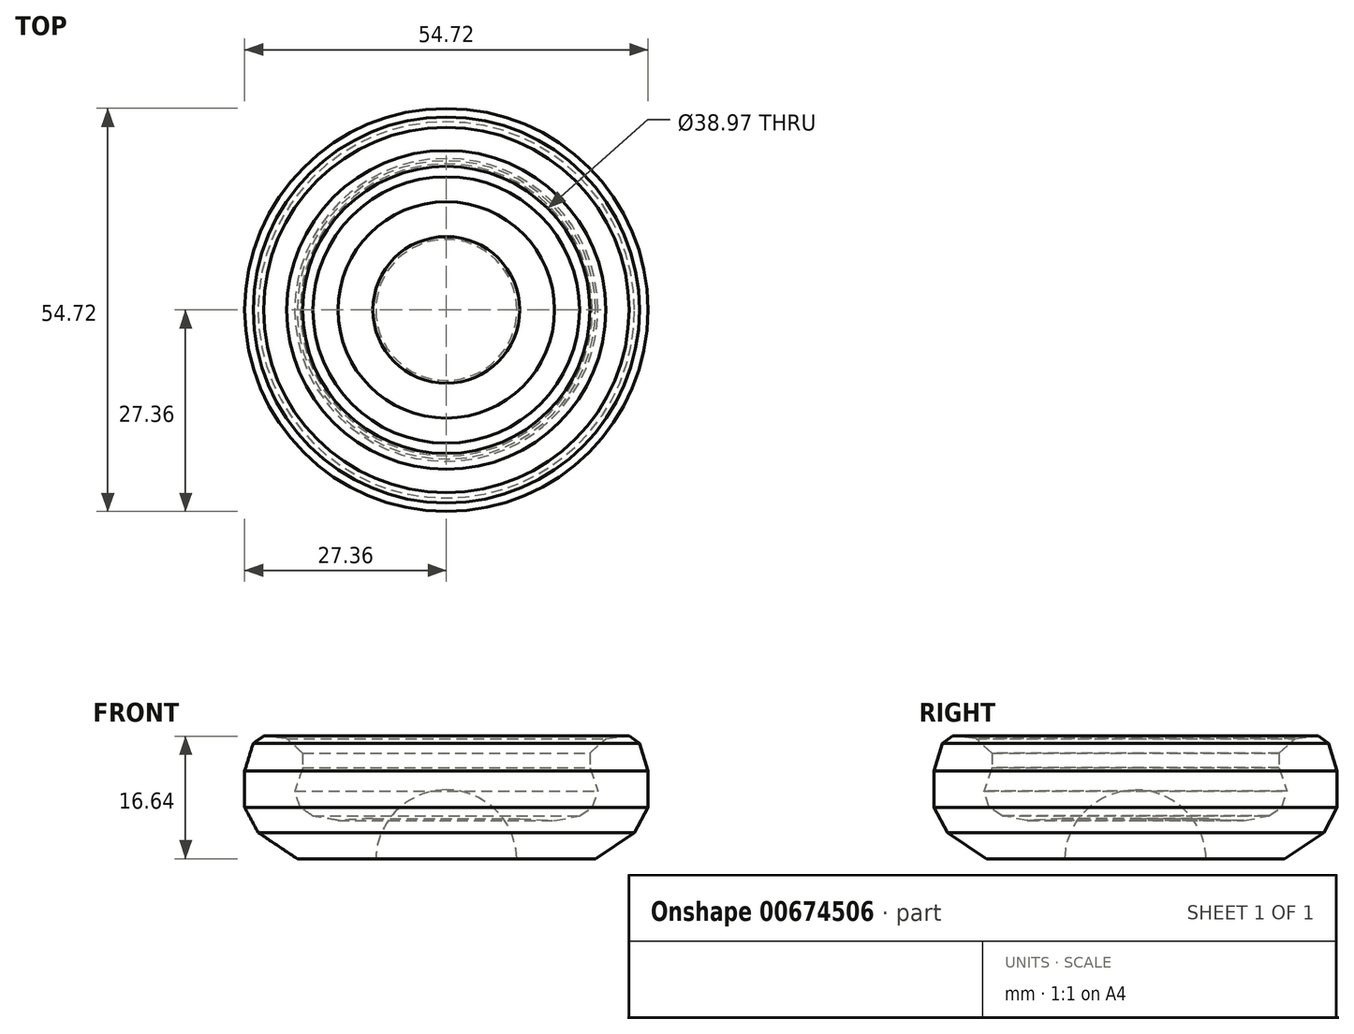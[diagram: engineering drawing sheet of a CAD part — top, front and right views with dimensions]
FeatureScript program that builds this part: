
annotation { "Feature Type Name" : "Feature", "Feature Type Description" : "" }
export const myFeature = defineFeature(function(context is Context, id is Id, definition is map)
    precondition{}
    {
        {
            var Q0;
            Q0=qCreatedBy(makeId("Front.planeOp"),FACE);
            var sketch = newSketch(context, id + "F0", { "sketchPlane" : qUnion([Q0])});
            skLineSegment(sketch, "E0", {"start": v(0, 0) * mm, "end": v(-20.23, 0) * mm});
            skLineSegment(sketch, "E1", {"start": v(-20.23, 0) * mm, "end": v(-25.53, 3.55) * mm});
            skLineSegment(sketch, "E2", {"start": v(-25.53, 3.55) * mm, "end": v(-27.36, 6.95) * mm});
            skLineSegment(sketch, "E3", {"start": v(-27.36, 6.95) * mm, "end": v(-27.36, 11.92) * mm});
            skLineSegment(sketch, "E4", {"start": v(-27.36, 11.92) * mm, "end": v(-26.2, 15.65) * mm});
            skLineSegment(sketch, "E5", {"start": v(-26.2, 15.65) * mm, "end": v(-24.79, 16.64) * mm});
            skLineSegment(sketch, "E6", {"start": v(-24.79, 16.64) * mm, "end": v(-21.64, 16.31) * mm});
            skLineSegment(sketch, "E7", {"start": v(-21.64, 16.31) * mm, "end": v(-19.49, 14.32) * mm});
            skLineSegment(sketch, "E8", {"start": v(-19.49, 14.32) * mm, "end": v(-19.49, 12.34) * mm});
            skLineSegment(sketch, "E9", {"start": v(-19.49, 12.34) * mm, "end": v(-20.56, 9.19) * mm});
            skLineSegment(sketch, "E10", {"start": v(-20.56, 9.19) * mm, "end": v(-19.82, 6.95) * mm});
            skLineSegment(sketch, "E11", {"start": v(-19.82, 6.95) * mm, "end": v(-18.08, 5.8) * mm});
            skLineSegment(sketch, "E12", {"start": v(-18.08, 5.8) * mm, "end": v(-14.68, 5.21) * mm});
            skLineSegment(sketch, "E13", {"start": v(-14.68, 5.21) * mm, "end": v(-9.96, 5.46) * mm});
            skLineSegment(sketch, "E14", {"start": v(-9.96, 5.46) * mm, "end": v(0, 5.46) * mm});
            skLineSegment(sketch, "E15", {"start": v(0, 5.46) * mm, "end": v(0, 0) * mm});
            skSolve(sketch);
        }
        {
            var Q0;
            Q0=sQuery(id+"F0.wireOp",EDGE,"E0");
            var Q1;
            Q1=sQuery(id+"F0.wireOp",EDGE,"E1");
            var Q2;
            Q2=sQuery(id+"F0.wireOp",EDGE,"E2");
            var Q3;
            Q3=sQuery(id+"F0.wireOp",EDGE,"E3");
            var Q4;
            Q4=sQuery(id+"F0.wireOp",EDGE,"E4");
            var Q5;
            Q5=sQuery(id+"F0.wireOp",EDGE,"E5");
            var Q6;
            Q6=sQuery(id+"F0.wireOp",EDGE,"E6");
            var Q7;
            Q7=sQuery(id+"F0.wireOp",EDGE,"E7");
            var Q8;
            Q8=sQuery(id+"F0.wireOp",EDGE,"E8");
            var Q9;
            Q9=sQuery(id+"F0.wireOp",EDGE,"E9");
            var Q10;
            Q10=sQuery(id+"F0.wireOp",EDGE,"E10");
            var Q11;
            Q11=sQuery(id+"F0.wireOp",EDGE,"E11");
            var Q12;
            Q12=sQuery(id+"F0.wireOp",EDGE,"E12");
            var Q13;
            Q13=sQuery(id+"F0.wireOp",EDGE,"E13");
            var Q14;
            Q14=sQuery(id+"F0.wireOp",EDGE,"E14");
            var Q15;
            Q15=sQuery(id+"F0.wireOp",EDGE,"E15");
            revolve(context, id + "F1", {"bodyType" : ToolBodyType.SURFACE, "surfaceEntities" : qUnion([Q0, Q1, Q2, Q3, Q4, Q5, Q6, Q7, Q8, Q9, Q10, Q11, Q12, Q13, Q14]), "axis" : qUnion([Q15]), "revolveType" : RevolveType.FULL});
        }
        {
            var Q0;
            Q0=qCreatedBy(makeId("Front.planeOp"),FACE);
            var sketch = newSketch(context, id + "F2", { "sketchPlane" : qUnion([Q0])});
            skLineSegment(sketch, "E16", {"start": v(0, 0) * mm, "end": v(-9.56, 0) * mm});
            skLineSegment(sketch, "E17", {"start": v(0, 0) * mm, "end": v(0, 9.35) * mm});
            skArc(sketch, "E18", {"start": v(0, 9.35) * mm, "mid": v(-6.68, 6.62) * mm, "end": v(-9.56, 0) * mm});
            skSolve(sketch);
        }
        {
            var Q0;
            Q0=sQuery(id+"F2.wireOp",EDGE,"E18");
            var Q1;
            Q1=sQuery(id+"F2.wireOp",EDGE,"E16");
            var Q2;
            Q2=sQuery(id+"F2.wireOp",EDGE,"E17");
            revolve(context, id + "F3", {"bodyType" : ToolBodyType.SURFACE, "surfaceEntities" : qUnion([Q0, Q1]), "axis" : qUnion([Q2]), "revolveType" : RevolveType.FULL});
        }
    });
